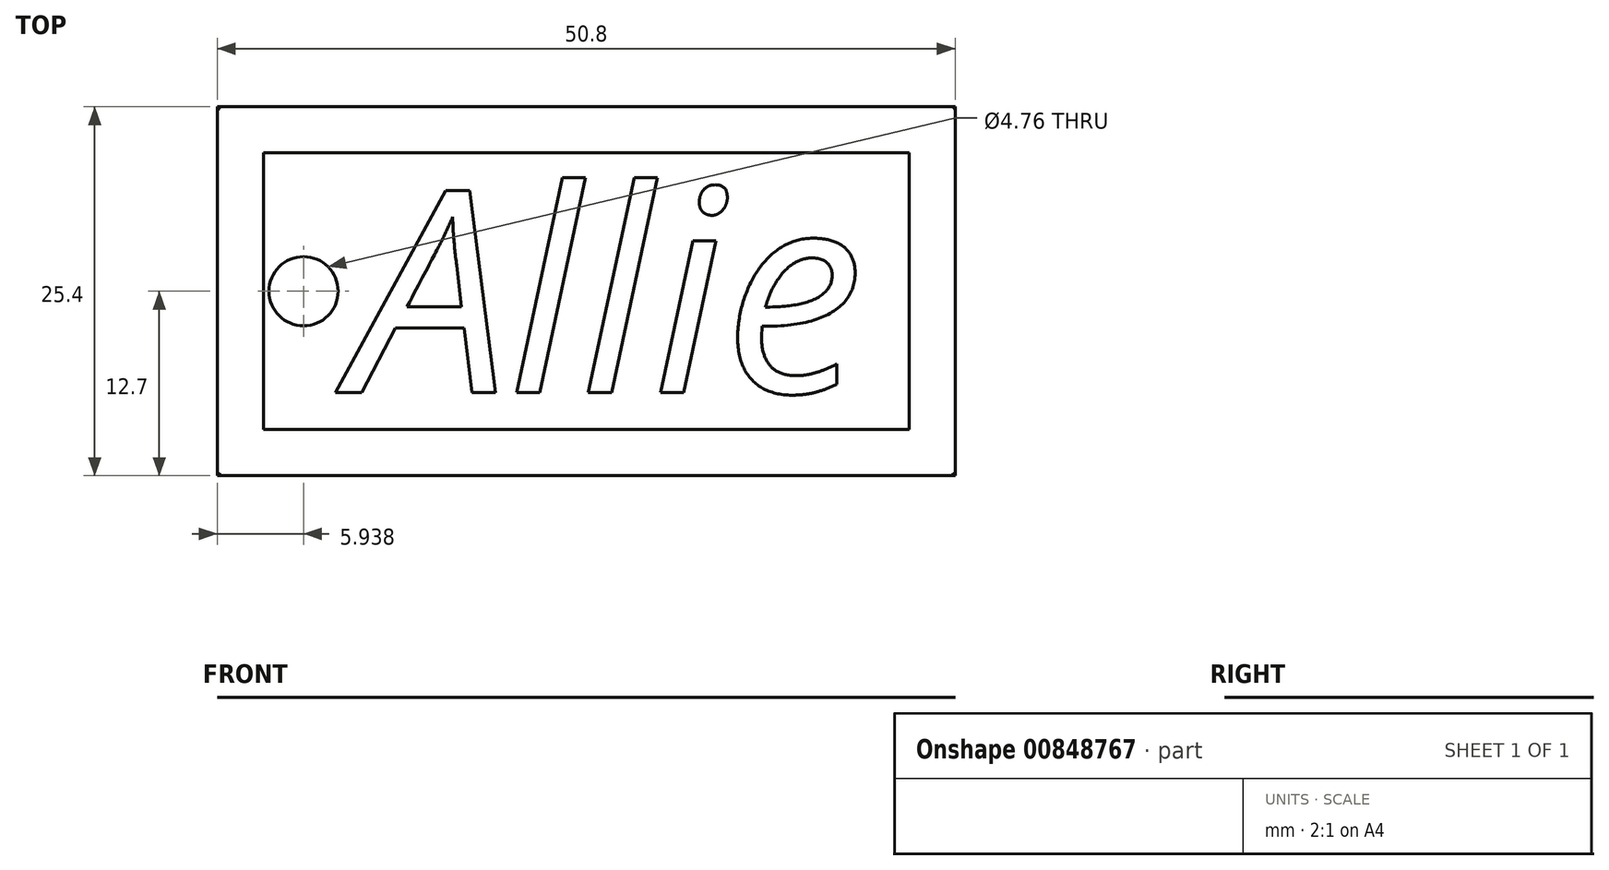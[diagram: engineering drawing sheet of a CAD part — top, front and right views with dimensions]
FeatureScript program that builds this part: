
annotation { "Feature Type Name" : "Feature", "Feature Type Description" : "" }
export const myFeature = defineFeature(function(context is Context, id is Id, definition is map)
    precondition{}
    {
        {
            var Q0;
            Q0=qCreatedBy(makeId("Top.planeOp"),FACE);
            var sketch = newSketch(context, id + "F0", { "sketchPlane" : qUnion([Q0])});
            skLineSegment(sketch, "E0.bottom", {"start": v(0, 0) * mm, "end": v(50.8, 0) * mm});
            skLineSegment(sketch, "E0.top", {"start": v(0, 25.4) * mm, "end": v(50.8, 25.4) * mm});
            skLineSegment(sketch, "E0.left", {"start": v(0, 0) * mm, "end": v(0, 25.4) * mm});
            skLineSegment(sketch, "E0.right", {"start": v(50.8, 0) * mm, "end": v(50.8, 25.4) * mm});
            skCircle(sketch, "E1", {"center": v(5.94, 12.7) * mm, "radius": 2.38 * mm});
            skPoint(sketch, "E1.centerSnap0", {"position": v(0, 12.7) * mm});
            skLineSegment(sketch, "E2.0", {"start": v(3.17, 22.23) * mm, "end": v(47.62, 22.23) * mm});
            skLineSegment(sketch, "E2.1", {"start": v(3.17, 3.18) * mm, "end": v(3.17, 22.23) * mm});
            skLineSegment(sketch, "E2.2", {"start": v(3.17, 3.18) * mm, "end": v(47.62, 3.18) * mm});
            skLineSegment(sketch, "E2.3", {"start": v(47.62, 3.18) * mm, "end": v(47.62, 22.23) * mm});
            skSolve(sketch);
        }
        {
            var Q0;
            Q0=makeQuery(id+"F0.imprint","IMPRINT",FACE,{"disambiguationData":[TD([[makeQuery(id+"F0.imprint","IMPRINT",EDGE,{"derivedFrom":sQuery(id+"F0.wireOp",EDGE,"E1")}),-1.0]])]});
            extrude(context, id + "F1", {"entities" : qUnion([Q0]), "depth" : 1 / 406.4 * mm, "offsetDistance" : 25.4 * mm});
        }
        {
            var Q0;
            Q0=qSketchRegion(id+"F0",true);
            extrude(context, id + "F2", {"entities" : qUnion([Q0]), "operationType" : NewBodyOperationType.ADD, "depth" : 1 / 203.2 * mm, "offsetDistance" : 25.4 * mm});
        }
        {
            var Q0;
            Q0=makeQuery(id+"F1.opExtrude","CAP_FACE",FACE,{"disambiguationData":[OSD([sQuery(id+"F0.wireOp",EDGE,"E1"),sQuery(id+"F0.wireOp",EDGE,"E2.0"),sQuery(id+"F0.wireOp",EDGE,"E2.1"),sQuery(id+"F0.wireOp",EDGE,"E2.2"),sQuery(id+"F0.wireOp",EDGE,"E2.3")])],"isStart":false});
            var sketch = newSketch(context, id + "F3", { "sketchPlane" : qUnion([Q0])});
            skText(sketch, "E3", { "text": "Allie\n", "fontName": "OpenSans-Italic.ttf"});
            const initialGuessF3  = {"E3": [0.00925, 0.00574, 1, 0, 0.01402]};
            skSetInitialGuess(sketch, initialGuessF3);
            skSolve(sketch);
        }
        {
            var Q0;
            Q0=qSketchRegion(id+"F3",true);
            extrude(context, id + "F4", {"entities" : qUnion([Q0]), "operationType" : NewBodyOperationType.ADD, "depth" : 1 / 812.8 * mm, "offsetDistance" : 25.4 * mm});
        }
        {
            var Q0;
            Q0=makeQuery(id+"F2.opExtrude","CAP_EDGE",EDGE,{"disambiguationData":[OSD([sQuery(id+"F0.wireOp",EDGE,"E0.bottom")])],"isStart":false});
            var Q1;
            Q1=makeQuery(id+"F2.opExtrude","CAP_EDGE",EDGE,{"disambiguationData":[OSD([sQuery(id+"F0.wireOp",EDGE,"E0.left")])],"isStart":false});
            var Q2;
            Q2=makeQuery(id+"F2.opExtrude","CAP_EDGE",EDGE,{"disambiguationData":[OSD([sQuery(id+"F0.wireOp",EDGE,"E0.top")])],"isStart":false});
            var Q3;
            Q3=makeQuery(id+"F2.opExtrude","CAP_EDGE",EDGE,{"disambiguationData":[OSD([sQuery(id+"F0.wireOp",EDGE,"E0.right")])],"isStart":false});
            fillet(context, id + "F5", {"entities" : qUnion([Q0, Q1, Q2, Q3]), "radius" : 2.54 * mm, "tangentPropagation" : true, "allowEdgeOverflow" : false});
        }
    });
